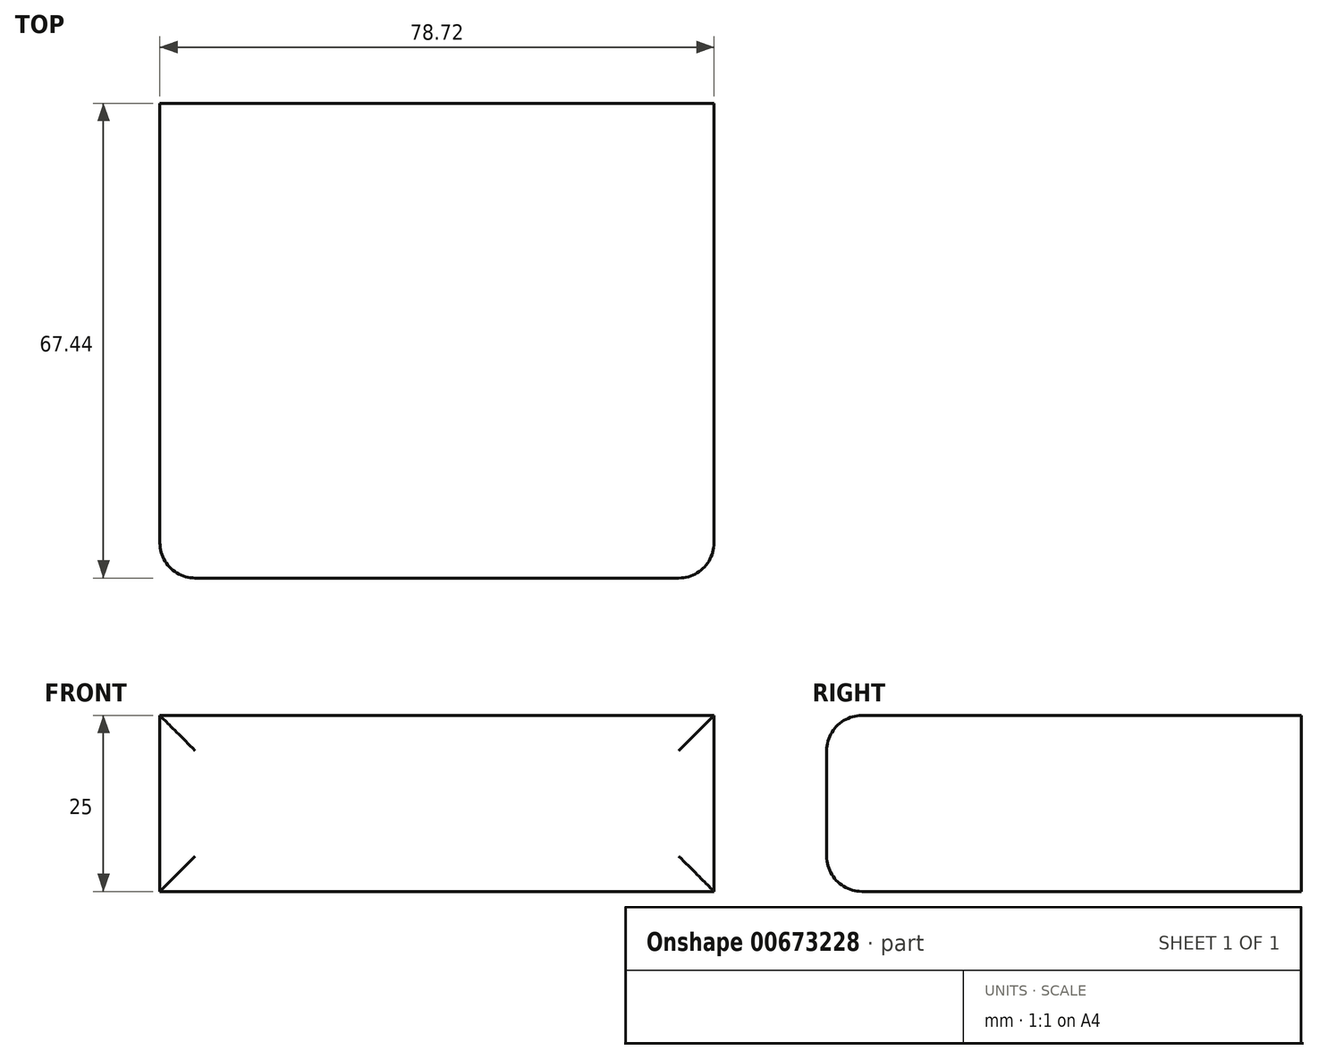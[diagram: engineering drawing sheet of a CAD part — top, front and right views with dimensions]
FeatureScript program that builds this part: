
annotation { "Feature Type Name" : "Feature", "Feature Type Description" : "" }
export const myFeature = defineFeature(function(context is Context, id is Id, definition is map)
    precondition{}
    {
        {
            var Q0;
            Q0=qCreatedBy(makeId("Top.planeOp"),FACE);
            var sketch = newSketch(context, id + "F0", { "sketchPlane" : qUnion([Q0])});
            skLineSegment(sketch, "E0.bottom", {"start": v(-38, 31.25) * mm, "end": v(40.72, 31.25) * mm});
            skLineSegment(sketch, "E0.top", {"start": v(-38, -36.19) * mm, "end": v(40.72, -36.19) * mm});
            skLineSegment(sketch, "E0.left", {"start": v(-38, 31.25) * mm, "end": v(-38, -36.19) * mm});
            skLineSegment(sketch, "E0.right", {"start": v(40.72, 31.25) * mm, "end": v(40.72, -36.19) * mm});
            skSolve(sketch);
        }
        {
            var Q0;
            Q0=makeQuery(id+"F0.imprint","IMPRINT",FACE,{"disambiguationData":[TD([[makeQuery(id+"F0.imprint","IMPRINT",EDGE,{"derivedFrom":sQuery(id+"F0.wireOp",EDGE,"E0.bottom")}),-1.0]])]});
            extrude(context, id + "F1", {"entities" : qUnion([Q0]), "depth" : 25 * mm, "offsetDistance" : 25 * mm});
        }
        {
            var Q0;
            Q0=makeQuery(id+"F1.opExtrude","SWEPT_FACE",FACE,{"disambiguationData":[OSD([sQuery(id+"F0.wireOp",EDGE,"E0.top")])]});
            fillet(context, id + "F2", {"entities" : qUnion([Q0]), "radius" : 5 * mm, "tangentPropagation" : true, "allowEdgeOverflow" : false});
        }
    });
